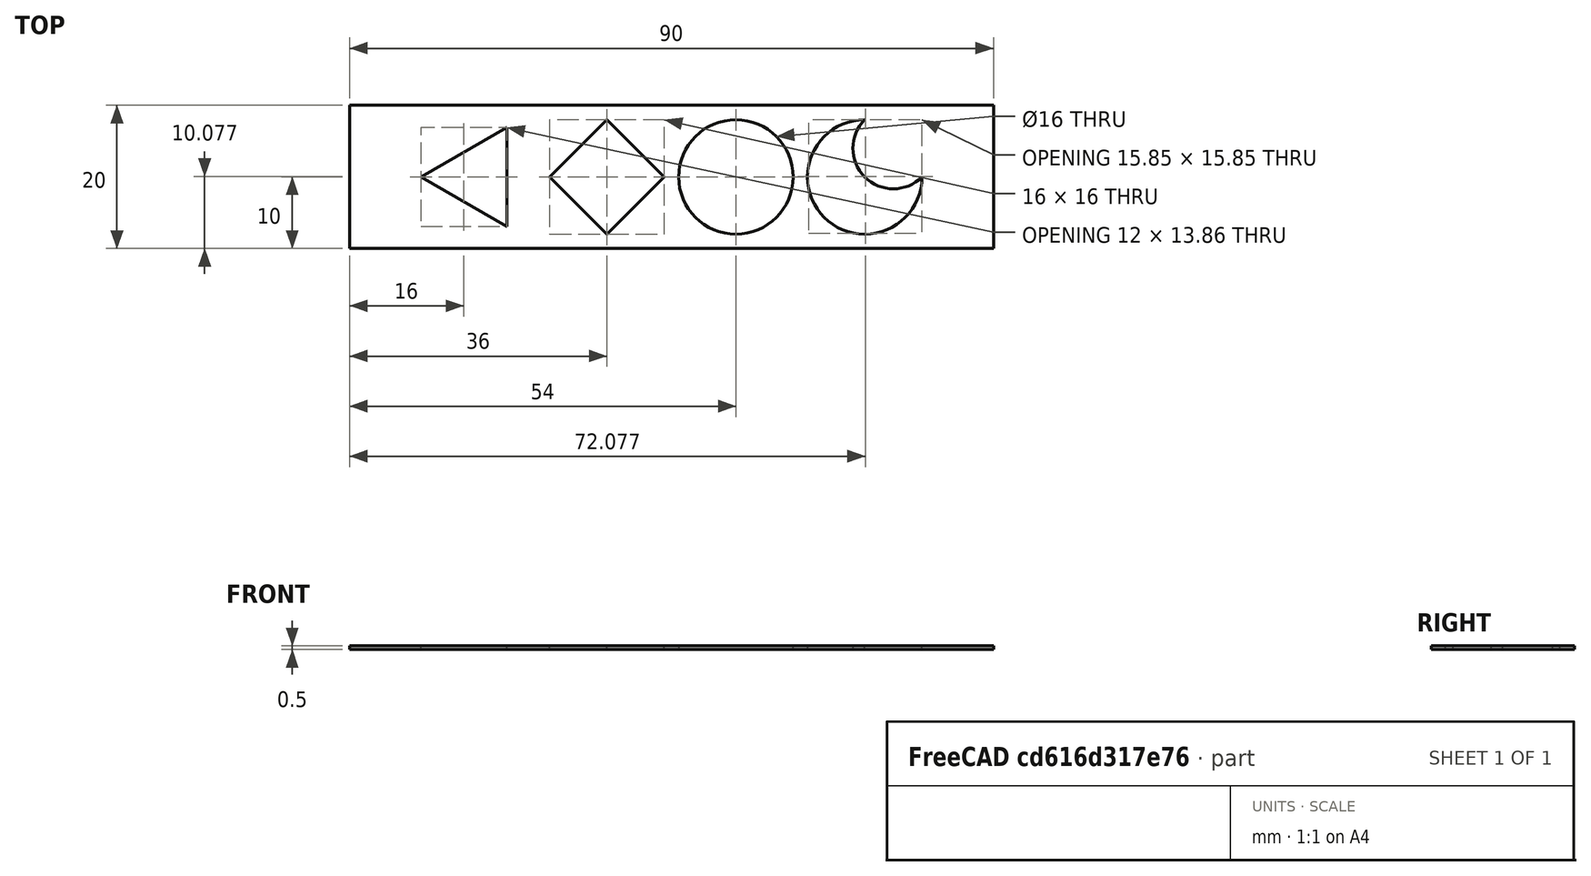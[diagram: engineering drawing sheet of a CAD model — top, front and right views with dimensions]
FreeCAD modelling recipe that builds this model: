
FCSTD DOCUMENT  (FreeCAD 0.17RUnknown)
Label: test104_testslice
License: All rights reserved
LicenseURL: http://en.wikipedia.org/wiki/All_rights_reserved
objects: Sketcher::SketchObject×1, PartDesign::Pad×1, PartDesign::Body×1
note: 4 computed .brp shape members not serialized (recipe doc carries the construction recipe); baked Part::Feature solids carry a one-line shape summary decoded from their .brp

FEATURE [Sketcher::SketchObject] Sketch
  MapMode = 5
  Support = -> [XY_Plane]
  sketch-geometry (20):
    g0: LineSegment StartX=0 StartY=20 StartZ=0 EndX=90 EndY=20 EndZ=0
    g1: LineSegment StartX=90 StartY=20 StartZ=0 EndX=90 EndY=0 EndZ=0
    g2: LineSegment StartX=90 StartY=0 StartZ=0 EndX=0 EndY=0 EndZ=0
    g3: LineSegment StartX=0 StartY=0 StartZ=0 EndX=0 EndY=20 EndZ=0
    g4: Circle CenterX=54 CenterY=10 CenterZ=0 NormalX=0 NormalY=0 NormalZ=1 AngleXU=0 Radius=8
    g5: LineSegment StartX=44 StartY=10 StartZ=0 EndX=36 EndY=18 EndZ=0
    g6: LineSegment StartX=36 StartY=18 StartZ=0 EndX=28 EndY=10 EndZ=0
    g7: LineSegment StartX=28 StartY=10 StartZ=0 EndX=36 EndY=2 EndZ=0
    g8: LineSegment StartX=36 StartY=2 StartZ=0 EndX=44 EndY=10 EndZ=0
    g9: Circle [constr] CenterX=36 CenterY=10 CenterZ=0 NormalX=0 NormalY=0 NormalZ=1 AngleXU=0 Radius=8
    g10: ArcOfCircle CenterX=72 CenterY=10 CenterZ=0 NormalX=0 NormalY=0 NormalZ=1 AngleXU=0 Radius=8 StartAngle=1.5708 EndAngle=6.28319
    g11: ArcOfCircle CenterX=76 CenterY=14 CenterZ=0 NormalX=0 NormalY=0 NormalZ=1 AngleXU=0 Radius=5.65685 StartAngle=2.35619 EndAngle=5.49779
    g12: LineSegment StartX=22 StartY=3.07182 StartZ=0 EndX=22 EndY=16.9282 EndZ=0
    g13: LineSegment StartX=22 StartY=16.9282 StartZ=0 EndX=10 EndY=10 EndZ=0
    g14: LineSegment StartX=10 StartY=10 StartZ=0 EndX=22 EndY=3.07182 EndZ=0
    g15: Circle [constr] CenterX=18 CenterY=10 CenterZ=0 NormalX=0 NormalY=0 NormalZ=1 AngleXU=0 Radius=8
    g16: LineSegment [constr] StartX=72 StartY=10 StartZ=0 EndX=80 EndY=10 EndZ=0
    g17: LineSegment [constr] StartX=72 StartY=10 StartZ=0 EndX=72 EndY=18 EndZ=0
    g18: LineSegment [constr] StartX=72 StartY=18 StartZ=0 EndX=80 EndY=10 EndZ=0
    g19: LineSegment [constr] StartX=0 StartY=10 StartZ=0 EndX=90 EndY=10 EndZ=0
  constraints (59):
    c: Coincident(g0,g1)
    c: Coincident(g1,g2)
    c: Coincident(g2,g3)
    c: Coincident(g3,g0)
    c: Horizontal(g0)
    c: Horizontal(g2)
    c: Vertical(g1)
    c: Vertical(g3)
    c: DistanceX(g0,g0) = 90
    c: DistanceY(g1,g1) = 20
    c: Coincident(g2,g-1)
    c: Coincident(g5,g6)
    c: Coincident(g6,g7)
    c: Coincident(g7,g8)
    c: Coincident(g8,g5)
    c: Equal(g5,g6)
    c: Equal(g5,g7)
    c: Equal(g5,g8)
    c: PointOnObject(g5,g9)
    c: PointOnObject(g6,g9)
    c: PointOnObject(g7,g9)
    c: PointOnObject(g8,g9)
    c: Coincident(g11,g10)
    c: Coincident(g11,g10)
    c: Coincident(g12,g13)
    c: Coincident(g13,g14)
    c: Coincident(g14,g12)
    c: Equal(g12,g13)
    c: Equal(g12,g14)
    c: PointOnObject(g12,g15)
    c: PointOnObject(g13,g15)
    c: PointOnObject(g14,g15)
    c: Distance(g15,g3) = 18
    c: Distance(g15,g9) = 18
    c: Distance(g9,g4) = 18
    c: Distance(g4,g10) = 18
    c: Distance(g10,g1) = 18
    c: Distance(g4,g2) = 10
    c: Radius(g10) = 8
    c: Radius(g4) = 8
    c: Radius(g9) = 8
    c: Radius(g15) = 8
    c: Angle(g2,g8) = 0.785398
    c: Coincident(g16,g10)
    c: Coincident(g16,g10)
    c: Coincident(g17,g10)
    c: Coincident(g17,g10)
    c: Horizontal(g16)
    c: Vertical(g17)
    c: Coincident(g18,g10)
    c: Coincident(g18,g10)
    c: PointOnObject(g11,g18)
    c: Vertical(g12)
    c: PointOnObject(g19,g3)
    c: PointOnObject(g19,g1)
    c: DistanceY(g-1,g19) = 10
    c: DistanceY(g1,g19) = 10
    c: PointOnObject(g10,g19)
    c: PointOnObject(g9,g19)
FEATURE [PartDesign::Pad] Pad
  Length = 0.5
  Length2 = 100
  Profile = -> Sketch
  Type = 0
FEATURE [PartDesign::Body] Body
  Group = -> [Sketch,Pad]
  Origin = -> Origin
  Tip = -> Pad
